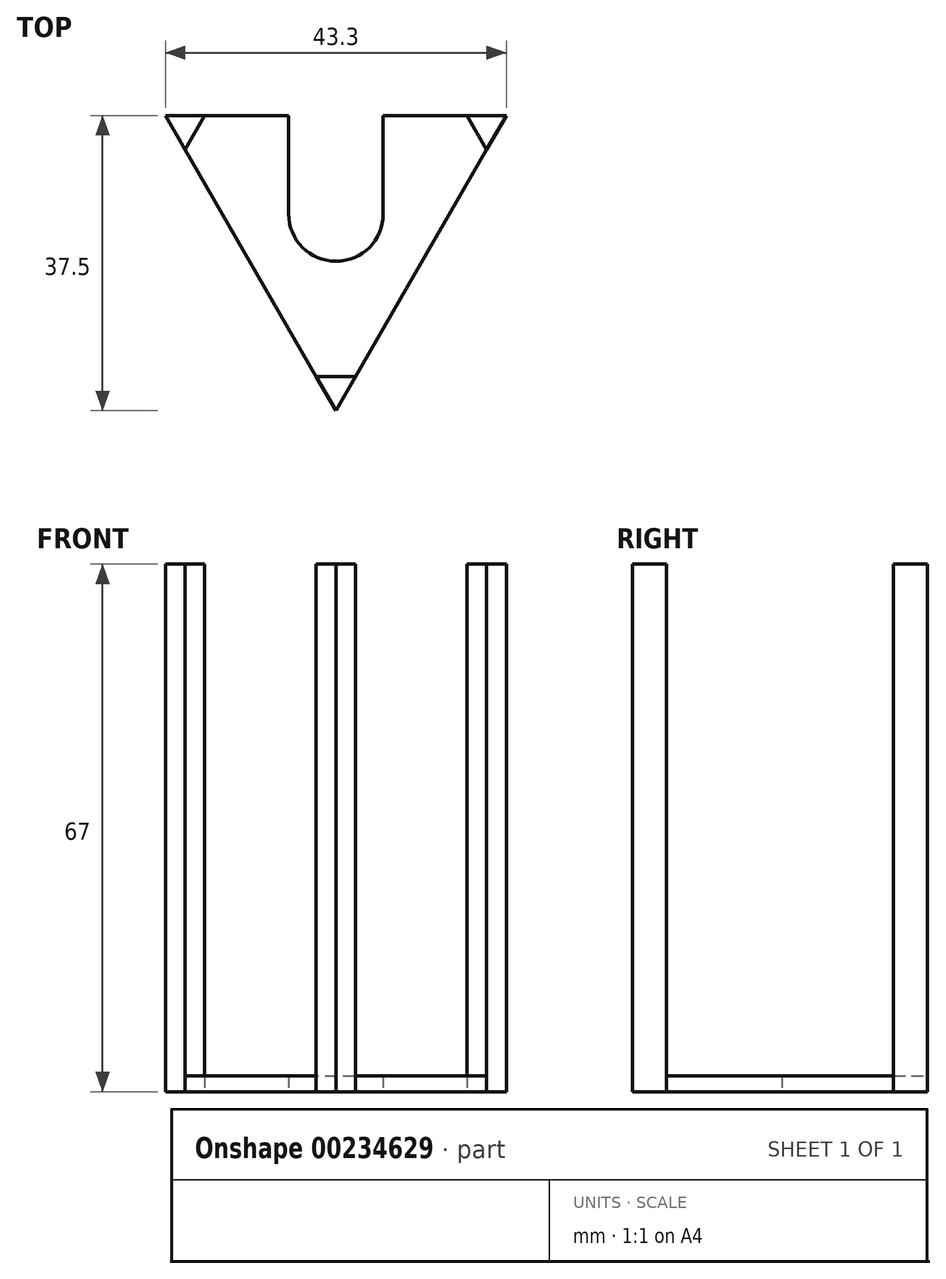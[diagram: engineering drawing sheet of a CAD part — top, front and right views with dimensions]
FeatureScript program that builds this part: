
annotation { "Feature Type Name" : "Feature", "Feature Type Description" : "" }
export const myFeature = defineFeature(function(context is Context, id is Id, definition is map)
    precondition{}
    {
        {
            var Q0;
            Q0=qCreatedBy(makeId("Top.planeOp"),FACE);
            var sketch = newSketch(context, id + "F0", { "sketchPlane" : qUnion([Q0])});
            skCircle(sketch, "E0.cCircle", {"center": v(0, 0) * mm, "radius": 12.5 * mm, "construction": true});
            skLineSegment(sketch, "E0.0", {"start": v(21.65, 12.5) * mm, "end": v(0, -25) * mm});
            skLineSegment(sketch, "E0.1", {"start": v(0, -25) * mm, "end": v(-21.65, 12.5) * mm});
            skLineSegment(sketch, "E0.2", {"start": v(-21.65, 12.5) * mm, "end": v(21.65, 12.5) * mm});
            skPoint(sketch, "E0.0.midPoint", {"position": v(10.83, -6.25) * mm});
            skPoint(sketch, "E1", {"position": v(-16.65, 12.5) * mm});
            skPoint(sketch, "E2", {"position": v(-19.15, 8.17) * mm});
            skLineSegment(sketch, "E3", {"start": v(-19.15, 8.17) * mm, "end": v(-16.65, 12.5) * mm});
            skLineSegment(sketch, "E4.1.0", {"start": v(2.5, -20.67) * mm, "end": v(-2.5, -20.67) * mm});
            skLineSegment(sketch, "E4.2.0", {"start": v(16.65, 12.5) * mm, "end": v(19.15, 8.17) * mm});
            skCircle(sketch, "E5", {"center": v(0, 0) * mm, "radius": 6 * mm});
            skLineSegment(sketch, "E6", {"start": v(-6, 0) * mm, "end": v(-6, 12.5) * mm});
            skLineSegment(sketch, "E7", {"start": v(6, 0) * mm, "end": v(6, 12.5) * mm});
            skSolve(sketch);
        }
        {
            var Q0;
            {var subQ3=sQuery(id+"F0.wireOp",EDGE,"E4.1.0");Q0=makeQuery(id+"F0.imprint","IMPRINT",FACE,{"disambiguationData":[TD([[makeQuery(id+"F0.imprint","IMPRINT",EDGE,{"derivedFrom":subQ3}),1.0]])]});}
            var Q1;
            {var subQ3=sQuery(id+"F0.wireOp",EDGE,"E3");Q1=makeQuery(id+"F0.imprint","IMPRINT",FACE,{"disambiguationData":[TD([[makeQuery(id+"F0.imprint","IMPRINT",EDGE,{"derivedFrom":subQ3}),1.0]])]});}
            var Q2;
            {var subQ3=sQuery(id+"F0.wireOp",EDGE,"E4.2.0");Q2=makeQuery(id+"F0.imprint","IMPRINT",FACE,{"disambiguationData":[TD([[makeQuery(id+"F0.imprint","IMPRINT",EDGE,{"derivedFrom":subQ3}),1.0]])]});}
            extrude(context, id + "F1", {"entities" : qUnion([Q0, Q1, Q2]), "depth" : 67 * mm});
        }
        {
            var Q0;
            {var subQ3=sQuery(id+"F0.wireOp",EDGE,"E3");Q0=makeQuery(id+"F0.imprint","IMPRINT",FACE,{"disambiguationData":[TD([[makeQuery(id+"F0.imprint","IMPRINT",EDGE,{"derivedFrom":subQ3}),-1.0]])]});}
            extrude(context, id + "F2", {"entities" : qUnion([Q0]), "depth" : 2 * mm});
        }
    });
